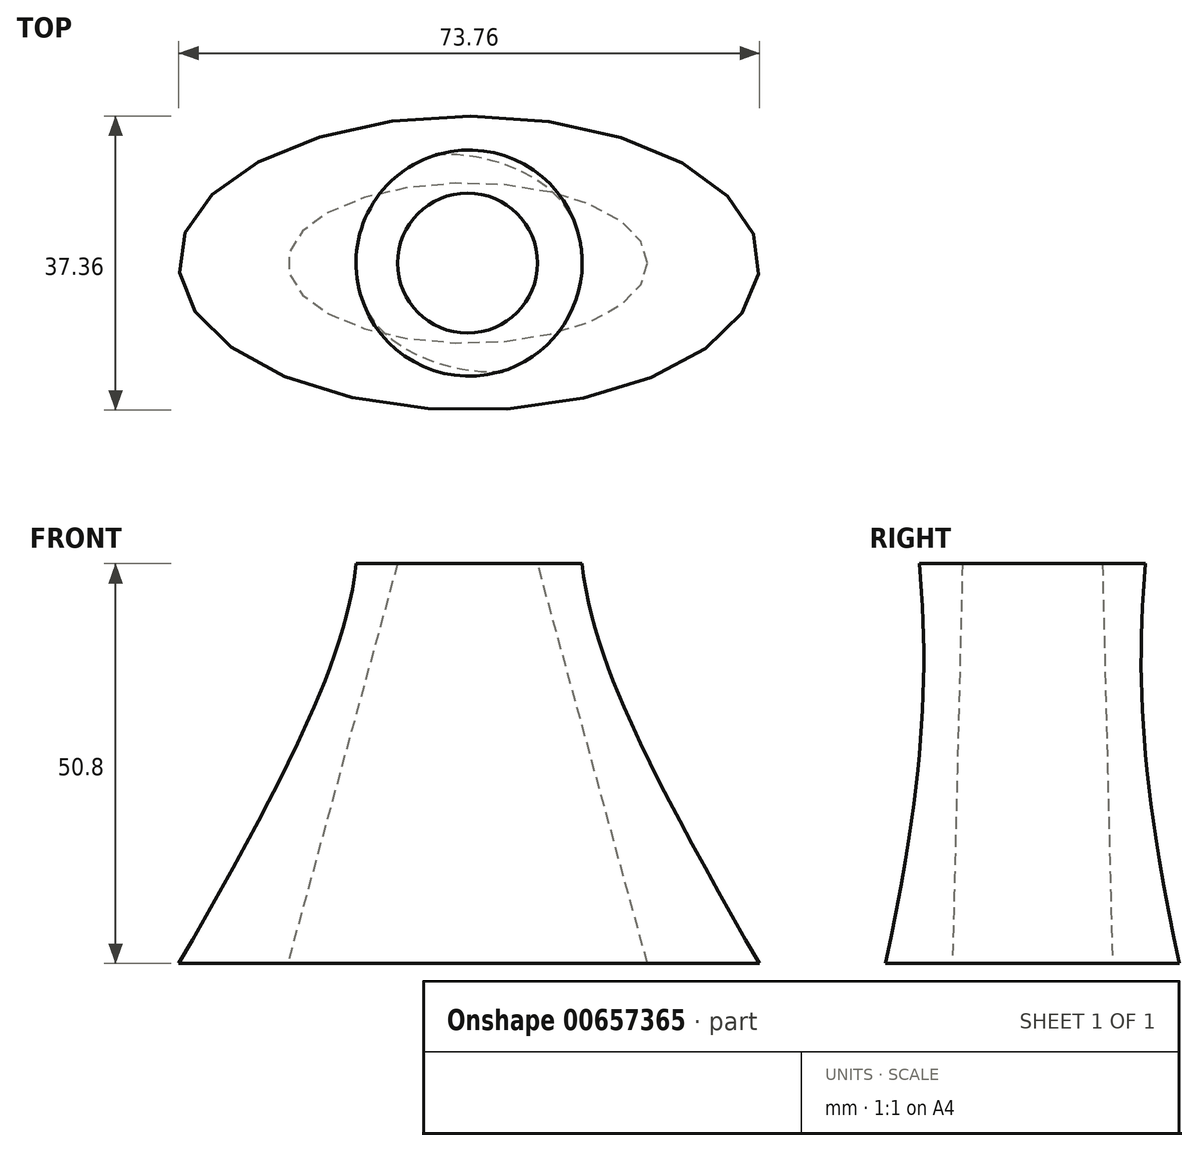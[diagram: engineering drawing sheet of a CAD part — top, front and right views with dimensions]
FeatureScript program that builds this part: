
annotation { "Feature Type Name" : "Feature", "Feature Type Description" : "" }
export const myFeature = defineFeature(function(context is Context, id is Id, definition is map)
    precondition{}
    {
        {
            var Q0;
            Q0=qCreatedBy(makeId("Top.planeOp"),FACE);
            cPlane(context, id + "F0", {"entities" : qUnion([Q0]), "cplaneType" : CPlaneType.OFFSET, "offset" : 50.8 * mm, "width" : 152.4 * mm, "height" : 152.4 * mm});
        }
        {
            var Q0;
            Q0=qCreatedBy(id+"F0.planeOp",FACE);
            var sketch = newSketch(context, id + "F1", { "sketchPlane" : qUnion([Q0])});
            skCircle(sketch, "E0", {"center": v(0, 0) * mm, "radius": 14.37 * mm});
            skSolve(sketch);
        }
        {
            var Q0;
            Q0=qCreatedBy(makeId("Top.planeOp"),FACE);
            var sketch = newSketch(context, id + "F2", { "sketchPlane" : qUnion([Q0])});
            skEllipse(sketch, "E1", {"center": v(0, 0) * mm, "majorRadius": 36.88 * mm, "minorRadius": 18.68 * mm, "majorAxis": v(1, 0)});
            skSolve(sketch);
        }
        {
            var Q0;
            Q0=qCreatedBy(id+"F0.planeOp",FACE);
            var sketch = newSketch(context, id + "F3", { "sketchPlane" : qUnion([Q0])});
            skLineSegment(sketch, "E2.bottom", {"start": v(35.93, 4.83) * mm, "end": v(20.76, 4.83) * mm});
            skLineSegment(sketch, "E2.top", {"start": v(35.93, -4.83) * mm, "end": v(20.76, -4.83) * mm});
            skLineSegment(sketch, "E2.left", {"start": v(35.93, 4.83) * mm, "end": v(35.93, -4.83) * mm});
            skLineSegment(sketch, "E2.right", {"start": v(20.76, 4.83) * mm, "end": v(20.76, -4.83) * mm});
            skPoint(sketch, "E2.middle", {"position": v(28.34, 0) * mm});
            skSolve(sketch);
        }
        {
            var Q0;
            Q0=makeQuery(id+"F3.imprint","IMPRINT",FACE,{"disambiguationData":[TD([[makeQuery(id+"F3.imprint","IMPRINT",EDGE,{"derivedFrom":sQuery(id+"F3.wireOp",EDGE,"E2.bottom")}),1.0]])]});
            extrude(context, id + "F4", {"entities" : qUnion([Q0]), "oppositeDirection" : true, "depth" : 76.2 * mm, "offsetDistance" : 25.4 * mm});
        }
        {
            var Q0;
            Q0=makeQuery(id+"F4.opExtrude","SWEPT_BODY",BODY,{"disambiguationData":[OSD([sQuery(id+"F3.wireOp",EDGE,"E2.bottom"),sQuery(id+"F3.wireOp",EDGE,"E2.top"),sQuery(id+"F3.wireOp",EDGE,"E2.left"),sQuery(id+"F3.wireOp",EDGE,"E2.right")])]});
            deleteBodies(context, id + "F5", {"entities" : qUnion([Q0])});
        }
        {
            var Q0;
            Q0=makeQuery(id+"F1.imprint","IMPRINT",FACE,{"disambiguationData":[TD([[makeQuery(id+"F1.imprint","IMPRINT",EDGE,{"derivedFrom":sQuery(id+"F1.wireOp",EDGE,"E0")}),1.0]])]});
            var Q1;
            Q1=makeQuery(id+"F2.imprint","IMPRINT",FACE,{"disambiguationData":[TD([[makeQuery(id+"F2.imprint","IMPRINT",EDGE,{"derivedFrom":sQuery(id+"F2.wireOp",EDGE,"E1")}),1.0]])]});
            loft(context, id + "F6", {"sheetProfilesArray" : [{ "sheetProfileEntities" : qUnion([Q0]) }, { "sheetProfileEntities" : qUnion([Q1]) }]});
        }
        {
            var Q0;
            Q0=qCreatedBy(id+"F0.planeOp",FACE);
            var sketch = newSketch(context, id + "F7", { "sketchPlane" : qUnion([Q0])});
            skCircle(sketch, "E3", {"center": v(63.42, 0) * mm, "radius": 8.9 * mm});
            skLineSegment(sketch, "E4", {"start": v(0, 0) * mm, "end": v(63.42, 0) * mm, "construction": true});
            skSolve(sketch);
        }
        {
            var Q0;
            Q0=qCreatedBy(makeId("Top.planeOp"),FACE);
            var sketch = newSketch(context, id + "F8", { "sketchPlane" : qUnion([Q0])});
            skEllipse(sketch, "E5", {"center": v(63.42, 0) * mm, "majorRadius": 22.86 * mm, "minorRadius": 10.16 * mm, "majorAxis": v(1, 0)});
            skSolve(sketch);
        }
        {
            var Q0;
            Q0=makeQuery(id+"F8.imprint","IMPRINT",FACE,{"disambiguationData":[TD([[makeQuery(id+"F8.imprint","IMPRINT",EDGE,{"derivedFrom":sQuery(id+"F8.wireOp",EDGE,"E5")}),1.0]])]});
            var Q1;
            Q1=makeQuery(id+"F7.imprint","IMPRINT",FACE,{"disambiguationData":[TD([[makeQuery(id+"F7.imprint","IMPRINT",EDGE,{"derivedFrom":sQuery(id+"F7.wireOp",EDGE,"E3")}),1.0]])]});
            loft(context, id + "F9", {"sheetProfilesArray" : [{ "sheetProfileEntities" : qUnion([Q0]) }, { "sheetProfileEntities" : qUnion([Q1]) }]});
        }
        {
            var Q0;
            Q0=qCreatedBy(makeId("Top.planeOp"),FACE);
            var sketch = newSketch(context, id + "F10", { "sketchPlane" : qUnion([Q0])});
            skLineSegment(sketch, "E6", {"start": v(63.6, 0) * mm, "end": v(0, 0) * mm});
            skSolve(sketch);
        }
        {
            var Q0;
            Q0=makeQuery(id+"F9.opLoft","SWEPT_BODY",BODY,{"disambiguationData":[OSD([makeQuery(id+"F7.imprint","IMPRINT",FACE,{"disambiguationData":[TD([[makeQuery(id+"F7.imprint","IMPRINT",EDGE,{"derivedFrom":sQuery(id+"F7.wireOp",EDGE,"E3")}),1.0]])]}),makeQuery(id+"F8.imprint","IMPRINT",FACE,{"disambiguationData":[TD([[makeQuery(id+"F8.imprint","IMPRINT",EDGE,{"derivedFrom":sQuery(id+"F8.wireOp",EDGE,"E5")}),1.0]])]})])]});
            var Q1;
            Q1=sQuery(id+"F10.wireOp",VERTEX,"E6.end");
            var Q2;
            Q2=sQuery(id+"F10.wireOp",EDGE,"E6");
            transform(context, id + "F11", {"entities" : qUnion([Q0]), "transformType" : TransformType.TRANSLATION_ENTITY, "oppositeDirectionEntity" : false, "transformLine" : qUnion([Q1, Q2]), "makeCopy" : false});
        }
        {
            var Q0;
            Q0=makeQuery(id+"F9.opLoft","SWEPT_BODY",BODY,{"disambiguationData":[OSD([makeQuery(id+"F7.imprint","IMPRINT",FACE,{"disambiguationData":[TD([[makeQuery(id+"F7.imprint","IMPRINT",EDGE,{"derivedFrom":sQuery(id+"F7.wireOp",EDGE,"E3")}),1.0]])]}),makeQuery(id+"F8.imprint","IMPRINT",FACE,{"disambiguationData":[TD([[makeQuery(id+"F8.imprint","IMPRINT",EDGE,{"derivedFrom":sQuery(id+"F8.wireOp",EDGE,"E5")}),1.0]])]})])]});
            var Q1;
            Q1=makeQuery(id+"F6.opLoft","SWEPT_BODY",BODY,{"disambiguationData":[OSD([makeQuery(id+"F1.imprint","IMPRINT",FACE,{"disambiguationData":[TD([[makeQuery(id+"F1.imprint","IMPRINT",EDGE,{"derivedFrom":sQuery(id+"F1.wireOp",EDGE,"E0")}),1.0]])]}),makeQuery(id+"F2.imprint","IMPRINT",FACE,{"disambiguationData":[TD([[makeQuery(id+"F2.imprint","IMPRINT",EDGE,{"derivedFrom":sQuery(id+"F2.wireOp",EDGE,"E1")}),1.0]])]})])]});
            booleanBodies(context, id + "F12", {"operationType" : BooleanOperationType.SUBTRACTION, "tools" : qUnion([Q0]), "targets" : qUnion([Q1])});
        }
    });
